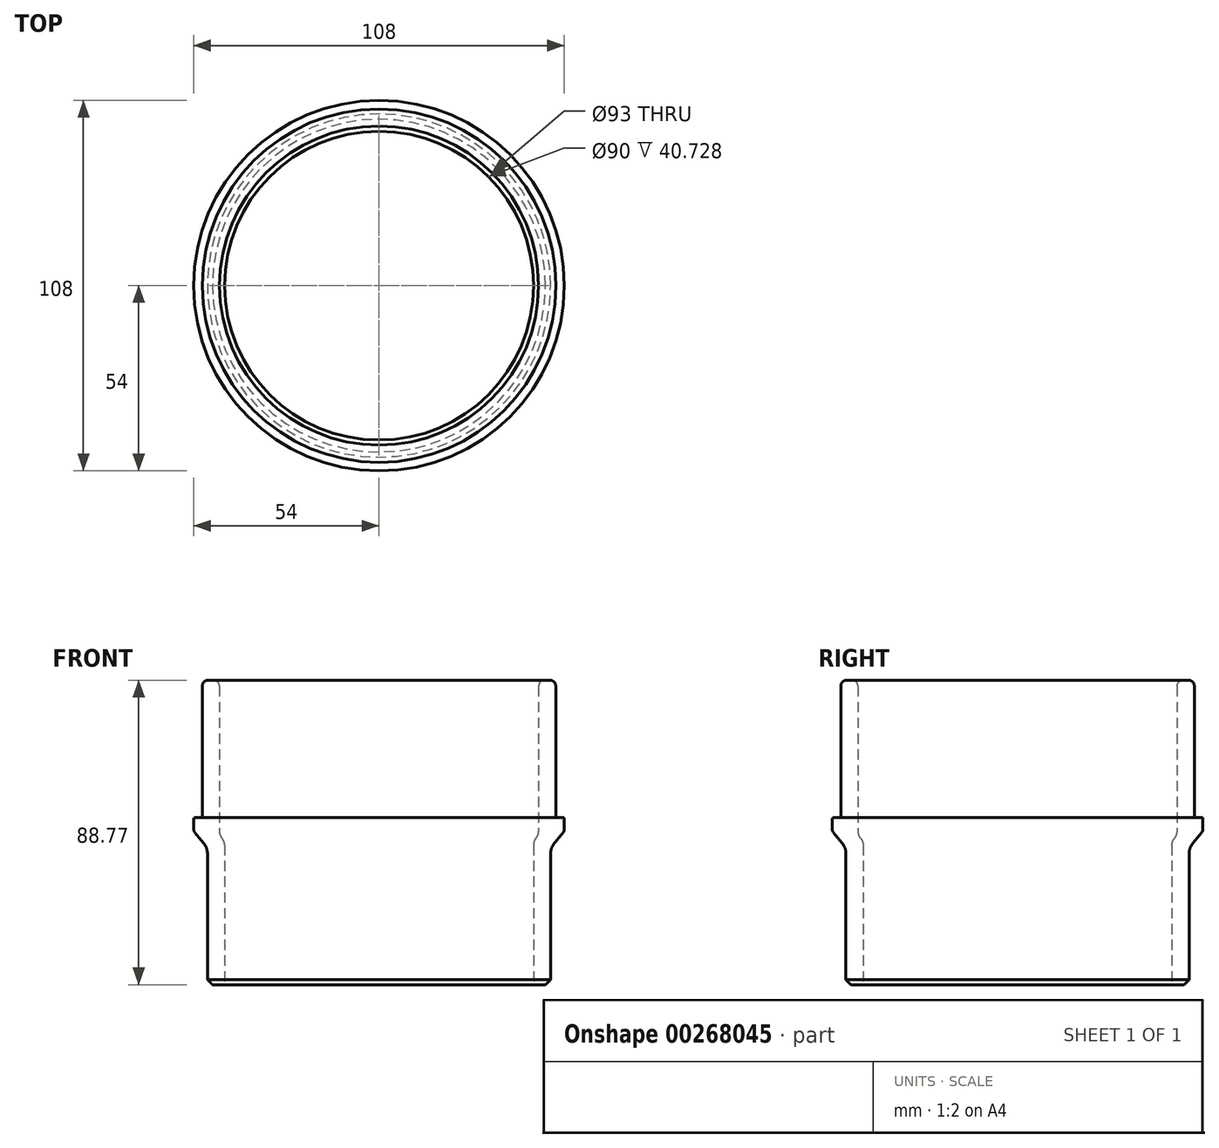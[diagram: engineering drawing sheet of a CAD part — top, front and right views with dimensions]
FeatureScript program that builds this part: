
annotation { "Feature Type Name" : "Feature", "Feature Type Description" : "" }
export const myFeature = defineFeature(function(context is Context, id is Id, definition is map)
    precondition{}
    {
        {
            var Q0;
            Q0=qCreatedBy(makeId("Front.planeOp"),FACE);
            var sketch = newSketch(context, id + "F0", { "sketchPlane" : qUnion([Q0])});
            skLineSegment(sketch, "E0", {"start": v(50, 0) * mm, "end": v(50, 40) * mm});
            skLineSegment(sketch, "E1", {"start": v(50, 40) * mm, "end": v(54, 44.77) * mm});
            skLineSegment(sketch, "E2", {"start": v(54, 44.77) * mm, "end": v(54, 48.77) * mm});
            skLineSegment(sketch, "E3", {"start": v(54, 48.77) * mm, "end": v(51.5, 48.77) * mm});
            skLineSegment(sketch, "E4", {"start": v(51.5, 48.77) * mm, "end": v(51.5, 88.77) * mm});
            skLineSegment(sketch, "E5", {"start": v(0, -37.25) * mm, "end": v(0, 130.62) * mm, "construction": true});
            skLineSegment(sketch, "E6", {"start": v(51.5, 88.77) * mm, "end": v(46.5, 88.77) * mm});
            skLineSegment(sketch, "E7", {"start": v(46.5, 88.77) * mm, "end": v(46.5, 43.6) * mm});
            skLineSegment(sketch, "E8", {"start": v(46.5, 43.6) * mm, "end": v(45, 41.82) * mm});
            skLineSegment(sketch, "E9", {"start": v(45, 41.82) * mm, "end": v(45, 0) * mm});
            skLineSegment(sketch, "E10", {"start": v(45, 0) * mm, "end": v(50, 0) * mm});
            skSolve(sketch);
        }
        {
            var Q0;
            Q0=makeQuery(id+"F0.imprint","IMPRINT",FACE,{"disambiguationData":[TD([[makeQuery(id+"F0.imprint","IMPRINT",EDGE,{"derivedFrom":sQuery(id+"F0.wireOp",EDGE,"E0")}),1.0]])]});
            var Q1;
            Q1=sQuery(id+"F0.wireOp",EDGE,"E5");
            revolve(context, id + "F1", {"entities" : qUnion([Q0]), "axis" : qUnion([Q1]), "revolveType" : RevolveType.FULL});
        }
        {
            var Q0;
            Q0=makeQuery(id+"F1.opRevolve","SWEPT_EDGE",EDGE,{"disambiguationData":[OSD([sQuery(id+"F0.wireOp",EDGE,"E4"),sQuery(id+"F0.wireOp",EDGE,"E6")])]});
            var Q1;
            Q1=makeQuery(id+"F1.opRevolve","SWEPT_EDGE",EDGE,{"disambiguationData":[OSD([sQuery(id+"F0.wireOp",EDGE,"E6"),sQuery(id+"F0.wireOp",EDGE,"E7")])]});
            var Q2;
            Q2=makeQuery(id+"F1.opRevolve","SWEPT_EDGE",EDGE,{"disambiguationData":[OSD([sQuery(id+"F0.wireOp",EDGE,"E1"),sQuery(id+"F0.wireOp",EDGE,"E2")])]});
            fillet(context, id + "F2", {"entities" : qUnion([Q0, Q1, Q2]), "radius" : 1.75 * mm, "tangentPropagation" : true, "defaultsChanged" : true, "vertexSettings" : [], "allowEdgeOverflow" : false});
        }
        {
            var Q0;
            Q0=makeQuery(id+"F1.opRevolve","SWEPT_EDGE",EDGE,{"disambiguationData":[OSD([sQuery(id+"F0.wireOp",EDGE,"E2"),sQuery(id+"F0.wireOp",EDGE,"E3")])]});
            var Q1;
            Q1=makeQuery(id+"F1.opRevolve","SWEPT_EDGE",EDGE,{"disambiguationData":[OSD([sQuery(id+"F0.wireOp",EDGE,"E3"),sQuery(id+"F0.wireOp",EDGE,"E4")])]});
            fillet(context, id + "F3", {"entities" : qUnion([Q0, Q1]), "radius" : 0.5 * mm, "tangentPropagation" : true, "allowEdgeOverflow" : false});
        }
        {
            var Q0;
            Q0=makeQuery(id+"F1.opRevolve","SWEPT_EDGE",EDGE,{"disambiguationData":[OSD([sQuery(id+"F0.wireOp",EDGE,"E0"),sQuery(id+"F0.wireOp",EDGE,"E1")])]});
            fillet(context, id + "F4", {"entities" : qUnion([Q0]), "radius" : 5 * mm, "tangentPropagation" : true, "allowEdgeOverflow" : false});
        }
        {
            var Q0;
            Q0=makeQuery(id+"F1.opRevolve","SWEPT_EDGE",EDGE,{"disambiguationData":[OSD([sQuery(id+"F0.wireOp",EDGE,"E0"),sQuery(id+"F0.wireOp",EDGE,"E10")])]});
            chamfer(context, id + "F5", {"entities" : qUnion([Q0]), "width" : 1.5 * mm, "tangentPropagation" : true});
        }
        {
            var Q0;
            Q0=makeQuery(id+"F1.opRevolve","SWEPT_EDGE",EDGE,{"disambiguationData":[OSD([sQuery(id+"F0.wireOp",EDGE,"E7"),sQuery(id+"F0.wireOp",EDGE,"E8")])]});
            var Q1;
            Q1=makeQuery(id+"F1.opRevolve","SWEPT_EDGE",EDGE,{"disambiguationData":[OSD([sQuery(id+"F0.wireOp",EDGE,"E8"),sQuery(id+"F0.wireOp",EDGE,"E9")])]});
            fillet(context, id + "F6", {"entities" : qUnion([Q0, Q1]), "radius" : 3 * mm, "tangentPropagation" : true, "allowEdgeOverflow" : false});
        }
    });
